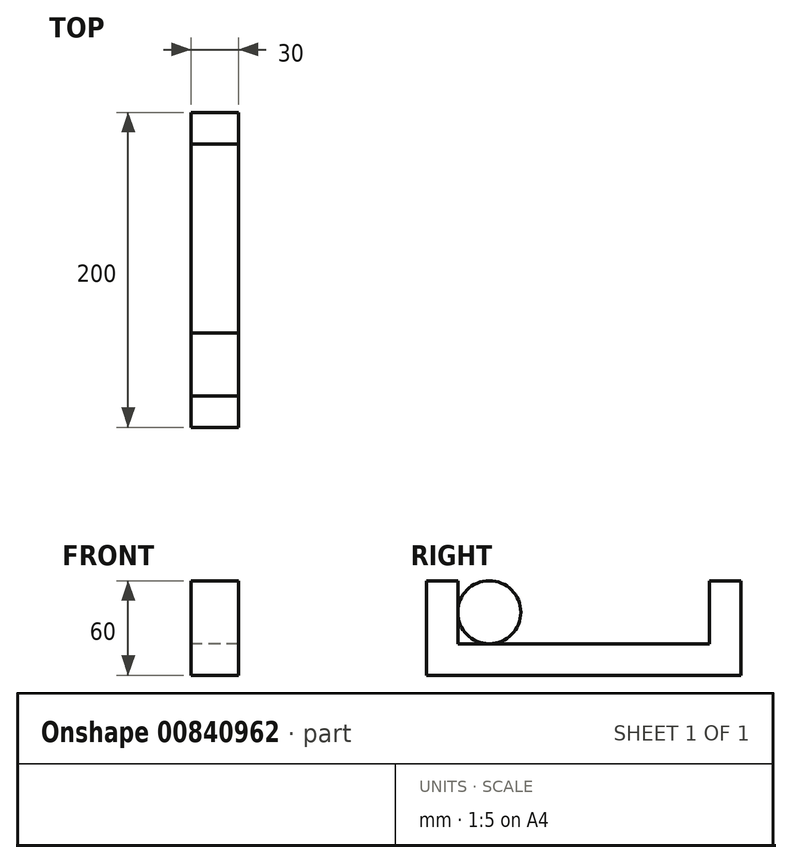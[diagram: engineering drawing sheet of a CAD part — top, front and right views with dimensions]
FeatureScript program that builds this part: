
annotation { "Feature Type Name" : "Feature", "Feature Type Description" : "" }
export const myFeature = defineFeature(function(context is Context, id is Id, definition is map)
    precondition{}
    {
        {
            var Q0;
            Q0=qCreatedBy(makeId("Right.planeOp"),FACE);
            var sketch = newSketch(context, id + "F0", { "sketchPlane" : qUnion([Q0])});
            skLineSegment(sketch, "E0.bottom", {"start": v(-100, 20) * mm, "end": v(-80, 20) * mm});
            skLineSegment(sketch, "E0.top", {"start": v(-100, -40) * mm, "end": v(100, -40) * mm});
            skLineSegment(sketch, "E0.left", {"start": v(-100, 20) * mm, "end": v(-100, -40) * mm});
            skLineSegment(sketch, "E0.right", {"start": v(100, 20) * mm, "end": v(100, -40) * mm});
            skLineSegment(sketch, "E1.top", {"start": v(-80, -20) * mm, "end": v(80, -20) * mm});
            skLineSegment(sketch, "E1.left", {"start": v(-80, 20) * mm, "end": v(-80, -20) * mm});
            skLineSegment(sketch, "E1.right", {"start": v(80, 20) * mm, "end": v(80, -20) * mm});
            skLineSegment(sketch, "E2.trimOffspring", {"start": v(80, 20) * mm, "end": v(100, 20) * mm});
            skCircle(sketch, "E3", {"center": v(-60, 0) * mm, "radius": 20 * mm});
            skSolve(sketch);
        }
        {
            var Q0;
            {var subQ0=sQuery(id+"F0.wireOp",EDGE,"E0.bottom");Q0=makeQuery(id+"F0.imprint","IMPRINT",FACE,{"disambiguationData":[TD([[makeQuery(id+"F0.imprint","IMPRINT",EDGE,{"derivedFrom":subQ0}),-1.0]])]});}
            var Q1;
            {var subQ0=sQuery(id+"F0.wireOp",EDGE,"E3");var subQ1=makeQuery(id+"F0.imprint","INTERSECT",VERTEX,{"derivedFrom":[sQuery(id+"F0.wireOp",EDGE,"E1.top"),subQ0]});Q1=makeQuery(id+"F0.imprint","IMPRINT",FACE,{"disambiguationData":[TD([[makeQuery(id+"F0.imprint","IMPRINT",EDGE,{"disambiguationData":[TD([[subQ1,1.0]])],"derivedFrom":subQ0}),1.0]])]});}
            extrude(context, id + "F1", {"entities" : qUnion([Q0, Q1]), "depth" : 30 * mm, "offsetDistance" : 25 * mm});
        }
    });
